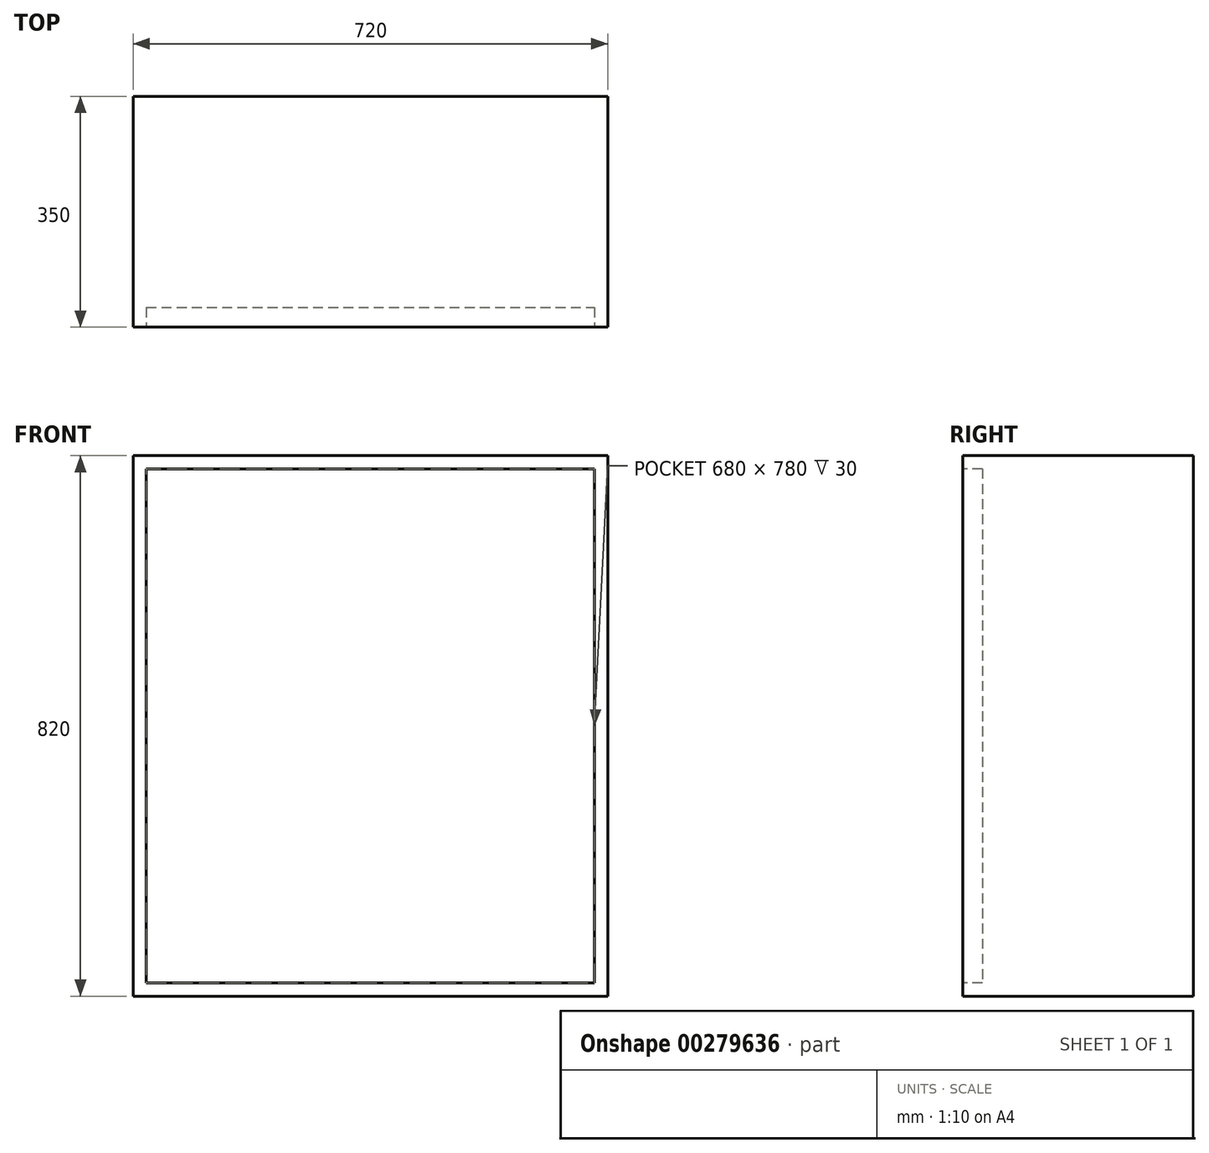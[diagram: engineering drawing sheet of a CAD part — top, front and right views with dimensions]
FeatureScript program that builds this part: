
annotation { "Feature Type Name" : "Feature", "Feature Type Description" : "" }
export const myFeature = defineFeature(function(context is Context, id is Id, definition is map)
    precondition{}
    {
        {
            var Q0;
            Q0=qCreatedBy(makeId("Top.planeOp"),FACE);
            var sketch = newSketch(context, id + "F0", { "sketchPlane" : qUnion([Q0])});
            skLineSegment(sketch, "E0.bottom", {"start": v(0, 0) * mm, "end": v(720, 0) * mm});
            skLineSegment(sketch, "E0.top", {"start": v(0, 350) * mm, "end": v(720, 350) * mm});
            skLineSegment(sketch, "E0.left", {"start": v(0, 0) * mm, "end": v(0, 350) * mm});
            skLineSegment(sketch, "E0.right", {"start": v(720, 0) * mm, "end": v(720, 350) * mm});
            skSolve(sketch);
        }
        {
            var Q0;
            Q0=makeQuery(id+"F0.imprint","IMPRINT",FACE,{"disambiguationData":[TD([[makeQuery(id+"F0.imprint","IMPRINT",EDGE,{"derivedFrom":sQuery(id+"F0.wireOp",EDGE,"E0.bottom")}),1.0]])]});
            extrude(context, id + "F1", {"entities" : qUnion([Q0]), "depth" : 820 * mm});
        }
        {
            var Q0;
            Q0=makeQuery(id+"F1.opExtrude","SWEPT_FACE",FACE,{"disambiguationData":[OSD([sQuery(id+"F0.wireOp",EDGE,"E0.bottom")])]});
            var sketch = newSketch(context, id + "F2", { "sketchPlane" : qUnion([Q0])});
            skLineSegment(sketch, "E1.0", {"start": v(20, 20) * mm, "end": v(700, 20) * mm});
            skLineSegment(sketch, "E1.1", {"start": v(20, 800) * mm, "end": v(20, 20) * mm});
            skLineSegment(sketch, "E1.2", {"start": v(700, 800) * mm, "end": v(20, 800) * mm});
            skLineSegment(sketch, "E1.3", {"start": v(700, 20) * mm, "end": v(700, 800) * mm});
            skLineSegment(sketch, "E2.0", {"start": v(-5, -5) * mm, "end": v(725, -5) * mm});
            skLineSegment(sketch, "E2.1", {"start": v(-5, 825) * mm, "end": v(-5, -5) * mm});
            skLineSegment(sketch, "E2.2", {"start": v(725, 825) * mm, "end": v(-5, 825) * mm});
            skLineSegment(sketch, "E2.3", {"start": v(725, -5) * mm, "end": v(725, 825) * mm});
            skSolve(sketch);
        }
        {
            var Q0;
            Q0=makeQuery(id+"F2.imprint","IMPRINT",FACE,{"disambiguationData":[TD([[makeQuery(id+"F2.imprint","IMPRINT",EDGE,{"derivedFrom":sQuery(id+"F2.wireOp",EDGE,"E1.0")}),1.0]])]});
            extrude(context, id + "F3", {"entities" : qUnion([Q0]), "operationType" : NewBodyOperationType.REMOVE, "oppositeDirection" : true, "depth" : 30 * mm});
        }
    });
